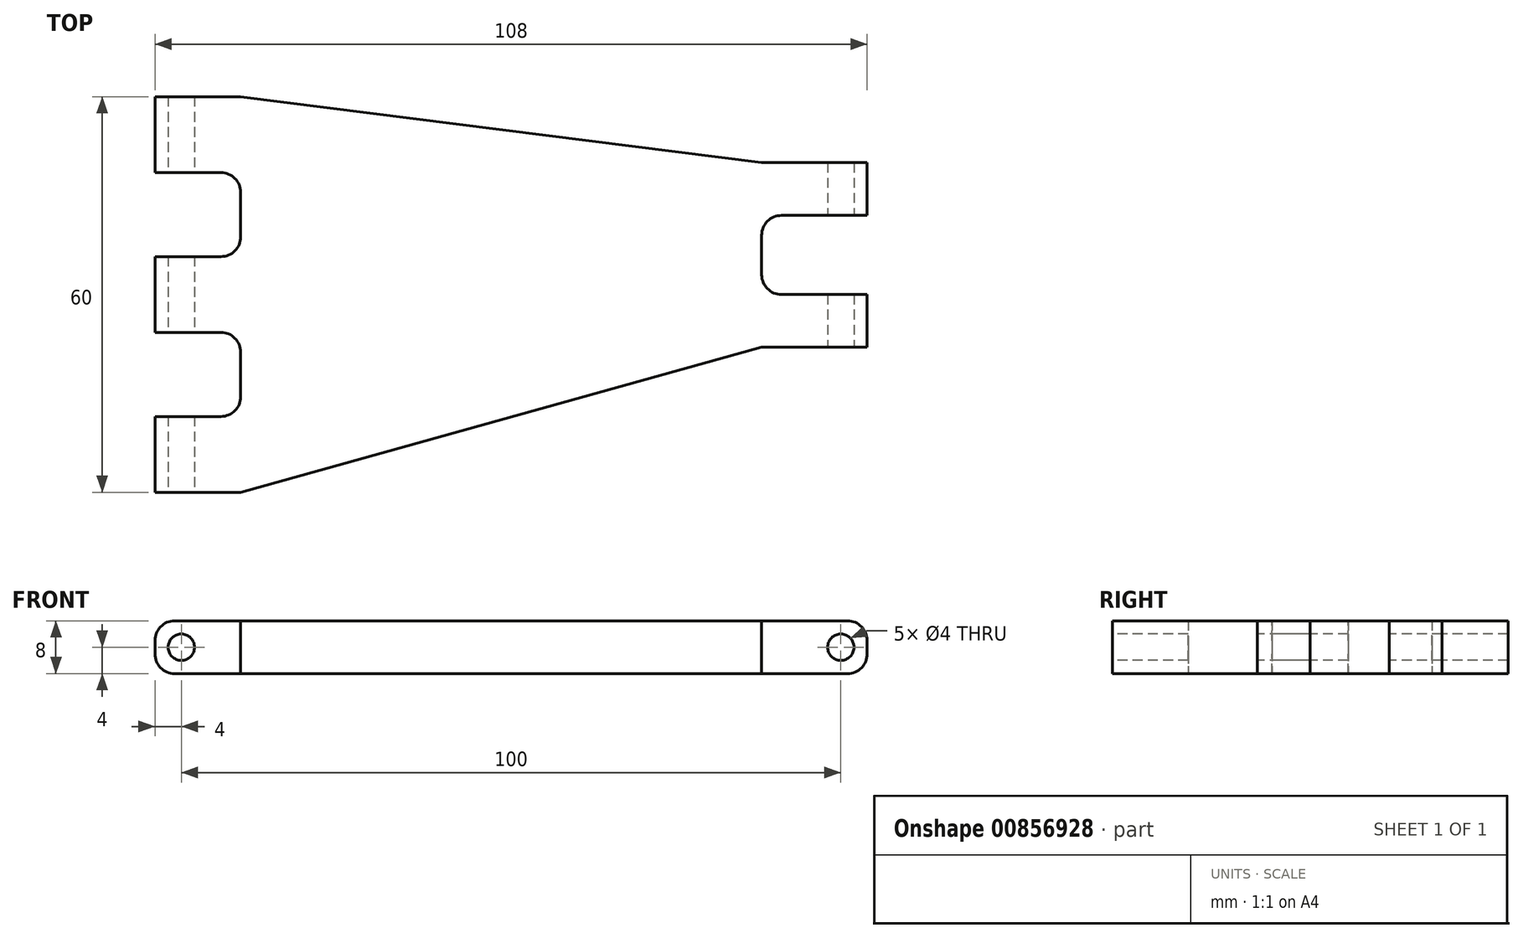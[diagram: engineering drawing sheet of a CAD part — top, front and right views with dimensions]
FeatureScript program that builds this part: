
annotation { "Feature Type Name" : "Feature", "Feature Type Description" : "" }
export const myFeature = defineFeature(function(context is Context, id is Id, definition is map)
    precondition{}
    {
        {
            var Q0;
            Q0=qCreatedBy(makeId("Top.planeOp"),FACE);
            var sketch = newSketch(context, id + "F0", { "sketchPlane" : qUnion([Q0])});
            skLineSegment(sketch, "E0.0", {"start": v(-4, 60) * mm, "end": v(-4, 48.5) * mm});
            skLineSegment(sketch, "E1.0", {"start": v(-4, 0) * mm, "end": v(-4, 11.5) * mm});
            skArc(sketch, "E2.0.0", {"start": v(6, 24.25) * mm, "mid": v(8.12, 23.37) * mm, "end": v(9, 21.25) * mm});
            skLineSegment(sketch, "E2.0.1", {"start": v(9, 21.25) * mm, "end": v(9, 14.5) * mm});
            skArc(sketch, "E2.0.2", {"start": v(9, 14.5) * mm, "mid": v(8.12, 12.38) * mm, "end": v(6, 11.5) * mm});
            skLineSegment(sketch, "E2.0.5", {"start": v(-4, 0) * mm, "end": v(9, 0) * mm});
            skArc(sketch, "E2.0.18", {"start": v(88, 39) * mm, "mid": v(88.88, 41.12) * mm, "end": v(91, 42) * mm});
            skLineSegment(sketch, "E2.0.21", {"start": v(104, 50) * mm, "end": v(88, 50) * mm});
            skLineSegment(sketch, "E3.0.3", {"start": v(6, 11.5) * mm, "end": v(-4, 11.5) * mm});
            skLineSegment(sketch, "E3.0.19", {"start": v(91, 42) * mm, "end": v(104, 42) * mm});
            skLineSegment(sketch, "E4.0.13", {"start": v(88, 22) * mm, "end": v(104, 22) * mm});
            skArc(sketch, "E4.0.16", {"start": v(91, 30) * mm, "mid": v(88.88, 30.88) * mm, "end": v(88, 33) * mm});
            skLineSegment(sketch, "E5", {"start": v(0, 0) * mm, "end": v(0, 65.17) * mm, "construction": true});
            skLineSegment(sketch, "E6", {"start": v(100, 65.3) * mm, "end": v(100, 5.57) * mm, "construction": true});
            skLineSegment(sketch, "E7", {"start": v(-4, 24.25) * mm, "end": v(6, 24.25) * mm});
            skLineSegment(sketch, "E8", {"start": v(104, 50) * mm, "end": v(104, 42) * mm});
            skLineSegment(sketch, "E9", {"start": v(104, 30) * mm, "end": v(104, 22) * mm});
            skLineSegment(sketch, "E10", {"start": v(100, 36) * mm, "end": v(135.8, 36) * mm, "construction": true});
            skLineSegment(sketch, "E11", {"start": v(88, 33) * mm, "end": v(88, 39) * mm});
            skLineSegment(sketch, "E12", {"start": v(91, 30) * mm, "end": v(104, 30) * mm});
            skLineSegment(sketch, "E13", {"start": v(9, 0) * mm, "end": v(88, 22) * mm});
            skLineSegment(sketch, "E14", {"start": v(-4, 60) * mm, "end": v(9, 60) * mm});
            skLineSegment(sketch, "E15", {"start": v(9, 60) * mm, "end": v(88, 50) * mm});
            skLineSegment(sketch, "E16", {"start": v(-4, 35.75) * mm, "end": v(6, 35.75) * mm});
            skLineSegment(sketch, "E17", {"start": v(9, 38.75) * mm, "end": v(9, 45.5) * mm});
            skLineSegment(sketch, "E18", {"start": v(6, 48.5) * mm, "end": v(-4, 48.5) * mm});
            skLineSegment(sketch, "E19.trimOffspring", {"start": v(-4, 35.75) * mm, "end": v(-4, 24.25) * mm});
            skPoint(sketch, "E20.visualSharp", {"position": v(9, 35.75) * mm});
            skArc(sketch, "E20.filletArc", {"start": v(6, 35.75) * mm, "mid": v(8.12, 36.63) * mm, "end": v(9, 38.75) * mm});
            skPoint(sketch, "E21.visualSharp", {"position": v(9, 48.5) * mm});
            skArc(sketch, "E21.filletArc", {"start": v(9, 45.5) * mm, "mid": v(8.12, 47.62) * mm, "end": v(6, 48.5) * mm});
            skLineSegment(sketch, "E22", {"start": v(-4, 30) * mm, "end": v(16.52, 30) * mm, "construction": true});
            skSolve(sketch);
        }
        {
            var Q0;
            Q0=makeQuery(id+"F0.imprint","IMPRINT",FACE,{"disambiguationData":[TD([[makeQuery(id+"F0.imprint","IMPRINT",EDGE,{"derivedFrom":sQuery(id+"F0.wireOp",EDGE,"E0.0")}),1.0]])]});
            extrude(context, id + "F1", {"entities" : qUnion([Q0]), "depth" : 8 * mm, "offsetDistance" : 25 * mm, "symmetric" : true});
        }
        {
            var Q0;
            Q0=makeQuery(id+"F1.opExtrude","SWEPT_FACE",FACE,{"disambiguationData":[OSD([sQuery(id+"F0.wireOp",EDGE,"E2.0.5"),sQuery(id+"F0.wireOp",EDGE,"E4.0.5")])]});
            var sketch = newSketch(context, id + "F2", { "sketchPlane" : qUnion([Q0])});
            skLineSegment(sketch, "E23", {"start": v(0, 0) * mm, "end": v(100, 0) * mm, "construction": true});
            skCircle(sketch, "E24", {"center": v(0, 0) * mm, "radius": 2 * mm});
            skCircle(sketch, "E25", {"center": v(100, 0) * mm, "radius": 2 * mm});
            skSolve(sketch);
        }
        {
            var Q0;
            Q0 = qSketchRegion(id + "F2", true);
            extrude(context, id + "F3", {"entities" : qUnion([Q0]), "operationType" : NewBodyOperationType.REMOVE, "endBound" : BoundingType.THROUGH_ALL, "oppositeDirection" : true, "depth" : 25 * mm, "offsetDistance" : 25 * mm});
        }
        {
            var Q0;
            Q0=makeQuery(id+"F1.opExtrude","CAP_EDGE",EDGE,{"disambiguationData":[OSD([sQuery(id+"F0.wireOp",EDGE,"E1.0")])],"isStart":false});
            var Q1;
            Q1=makeQuery(id+"F1.opExtrude","CAP_EDGE",EDGE,{"disambiguationData":[OSD([sQuery(id+"F0.wireOp",EDGE,"E19.trimOffspring")])],"isStart":false});
            var Q2;
            Q2=makeQuery(id+"F1.opExtrude","CAP_EDGE",EDGE,{"disambiguationData":[OSD([sQuery(id+"F0.wireOp",EDGE,"E0.0")])],"isStart":false});
            var Q3;
            Q3=makeQuery(id+"F1.opExtrude","CAP_EDGE",EDGE,{"disambiguationData":[OSD([sQuery(id+"F0.wireOp",EDGE,"E1.0")])],"isStart":true});
            var Q4;
            Q4=makeQuery(id+"F1.opExtrude","CAP_EDGE",EDGE,{"disambiguationData":[OSD([sQuery(id+"F0.wireOp",EDGE,"E19.trimOffspring")])],"isStart":true});
            var Q5;
            Q5=makeQuery(id+"F1.opExtrude","CAP_EDGE",EDGE,{"disambiguationData":[OSD([sQuery(id+"F0.wireOp",EDGE,"E0.0")])],"isStart":true});
            var Q6;
            Q6=makeQuery(id+"F1.opExtrude","CAP_EDGE",EDGE,{"disambiguationData":[OSD([sQuery(id+"F0.wireOp",EDGE,"E8")])],"isStart":true});
            var Q7;
            Q7=makeQuery(id+"F1.opExtrude","CAP_EDGE",EDGE,{"disambiguationData":[OSD([sQuery(id+"F0.wireOp",EDGE,"E9")])],"isStart":true});
            var Q8;
            Q8=makeQuery(id+"F1.opExtrude","CAP_EDGE",EDGE,{"disambiguationData":[OSD([sQuery(id+"F0.wireOp",EDGE,"E9")])],"isStart":false});
            var Q9;
            Q9=makeQuery(id+"F1.opExtrude","CAP_EDGE",EDGE,{"disambiguationData":[OSD([sQuery(id+"F0.wireOp",EDGE,"E8")])],"isStart":false});
            fillet(context, id + "F4", {"entities" : qUnion([Q0, Q1, Q2, Q3, Q4, Q5, Q6, Q7, Q8, Q9]), "radius" : 3 * mm, "tangentPropagation" : true, "allowEdgeOverflow" : false});
        }
    });
